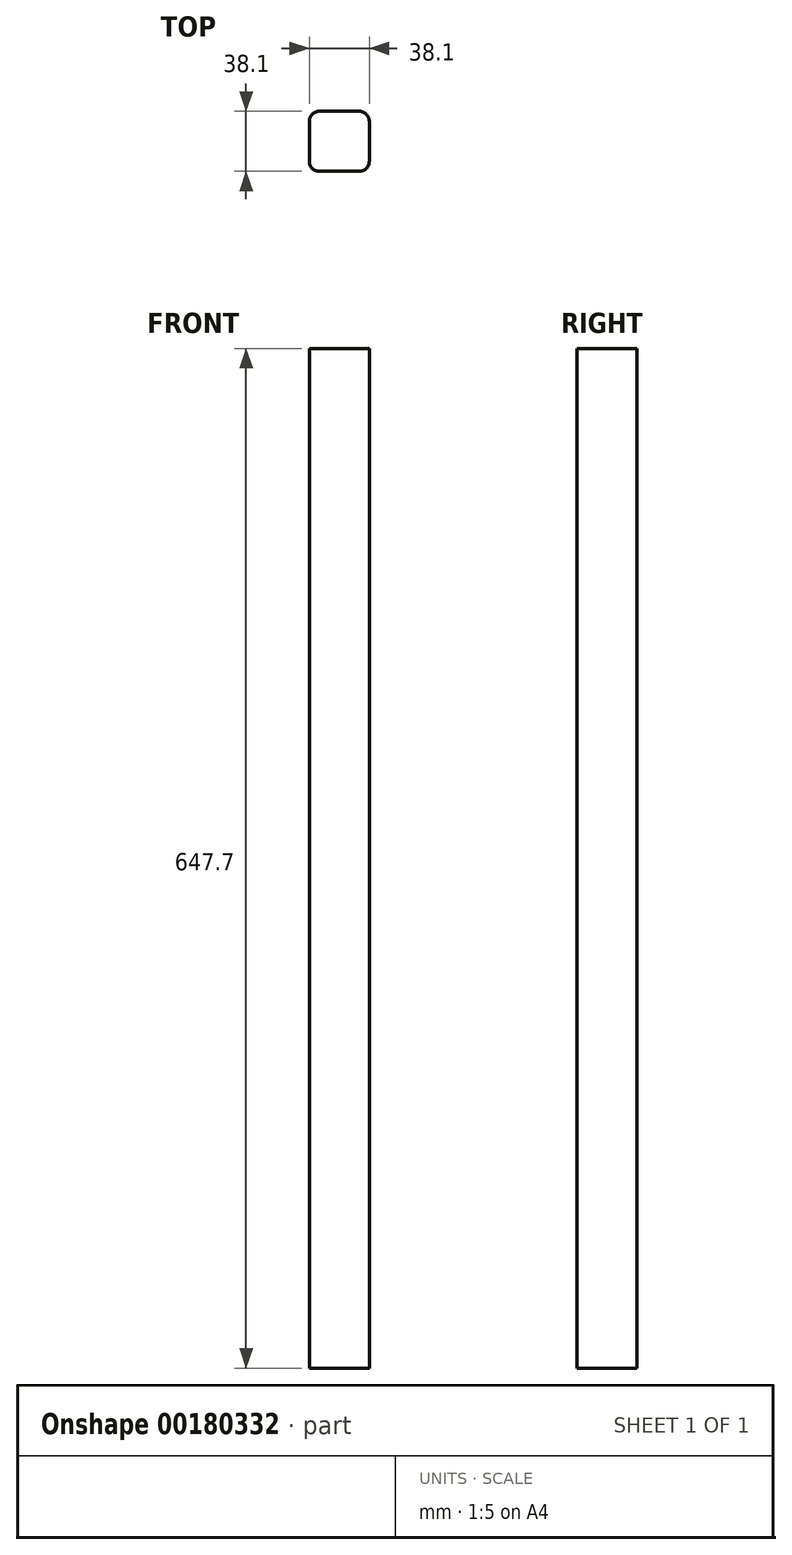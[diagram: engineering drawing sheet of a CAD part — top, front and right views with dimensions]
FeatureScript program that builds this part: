
annotation { "Feature Type Name" : "Feature", "Feature Type Description" : "" }
export const myFeature = defineFeature(function(context is Context, id is Id, definition is map)
    precondition{}
    {
        {
            var Q0;
            Q0=qCreatedBy(makeId("Top.planeOp"),FACE);
            var sketch = newSketch(context, id + "F0", { "sketchPlane" : qUnion([Q0])});
            skLineSegment(sketch, "E0.bottom", {"start": v(19.05, 19.05) * mm, "end": v(-19.05, 19.05) * mm});
            skLineSegment(sketch, "E0.top", {"start": v(19.05, -19.05) * mm, "end": v(-19.05, -19.05) * mm});
            skLineSegment(sketch, "E0.left", {"start": v(19.05, 19.05) * mm, "end": v(19.05, -19.05) * mm});
            skLineSegment(sketch, "E0.right", {"start": v(-19.05, 19.05) * mm, "end": v(-19.05, -19.05) * mm});
            skPoint(sketch, "E0.middle", {"position": v(0, 0) * mm});
            skSolve(sketch);
        }
        {
            var Q0;
            Q0 = qSketchRegion(id + "F0", true);
            extrude(context, id + "F1", {"entities" : qUnion([Q0]), "depth" : 647.7 * mm});
        }
        {
            var Q0;
            Q0=makeQuery(id+"F1.opExtrude","SWEPT_EDGE",EDGE,{"disambiguationData":[OSD([sQuery(id+"F0.wireOp",EDGE,"E0.bottom"),sQuery(id+"F0.wireOp",EDGE,"E0.right")])]});
            var Q1;
            Q1=makeQuery(id+"F1.opExtrude","SWEPT_EDGE",EDGE,{"disambiguationData":[OSD([sQuery(id+"F0.wireOp",EDGE,"E0.top"),sQuery(id+"F0.wireOp",EDGE,"E0.right")])]});
            var Q2;
            Q2=makeQuery(id+"F1.opExtrude","SWEPT_EDGE",EDGE,{"disambiguationData":[OSD([sQuery(id+"F0.wireOp",EDGE,"E0.bottom"),sQuery(id+"F0.wireOp",EDGE,"E0.left")])]});
            var Q3;
            Q3=makeQuery(id+"F1.opExtrude","SWEPT_EDGE",EDGE,{"disambiguationData":[OSD([sQuery(id+"F0.wireOp",EDGE,"E0.top"),sQuery(id+"F0.wireOp",EDGE,"E0.left")])]});
            fillet(context, id + "F2", {"entities" : qUnion([Q0, Q1, Q2, Q3]), "radius" : 6.35 * mm, "tangentPropagation" : true, "allowEdgeOverflow" : false});
        }
    });
